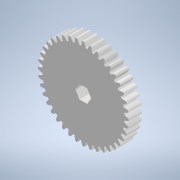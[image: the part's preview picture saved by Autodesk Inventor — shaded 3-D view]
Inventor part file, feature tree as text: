
AUTODESK INVENTOR PART (.ipt)
format: ipt  version: 2022 (Build 260153000, 153)  size: 2,217,984 bytes
history: native  units: mm
features: extrude x2, sketch x2
ambient origin geometry x8: Origin, YZ Plane, XZ Plane, XY Plane, X Axis, Y Axis, Z Axis, Center Point
bodies: Solid1 (feature_tree)
feature tree (4):
  extrude  "Extrusion1"  Depth=6.2mm
  extrude  "Extrusion2"  Depth=6.2mm TaperAngle=0.0deg
  sketch  "Sketch4"  dims[d5=6.2mm d6=0.0mm d7=3.1mm]
  sketch  "Sketch5"  dims[d8=60.0mm d10=360.0deg d12=6.2mm d13=0.0mm d14=0.45mm]
